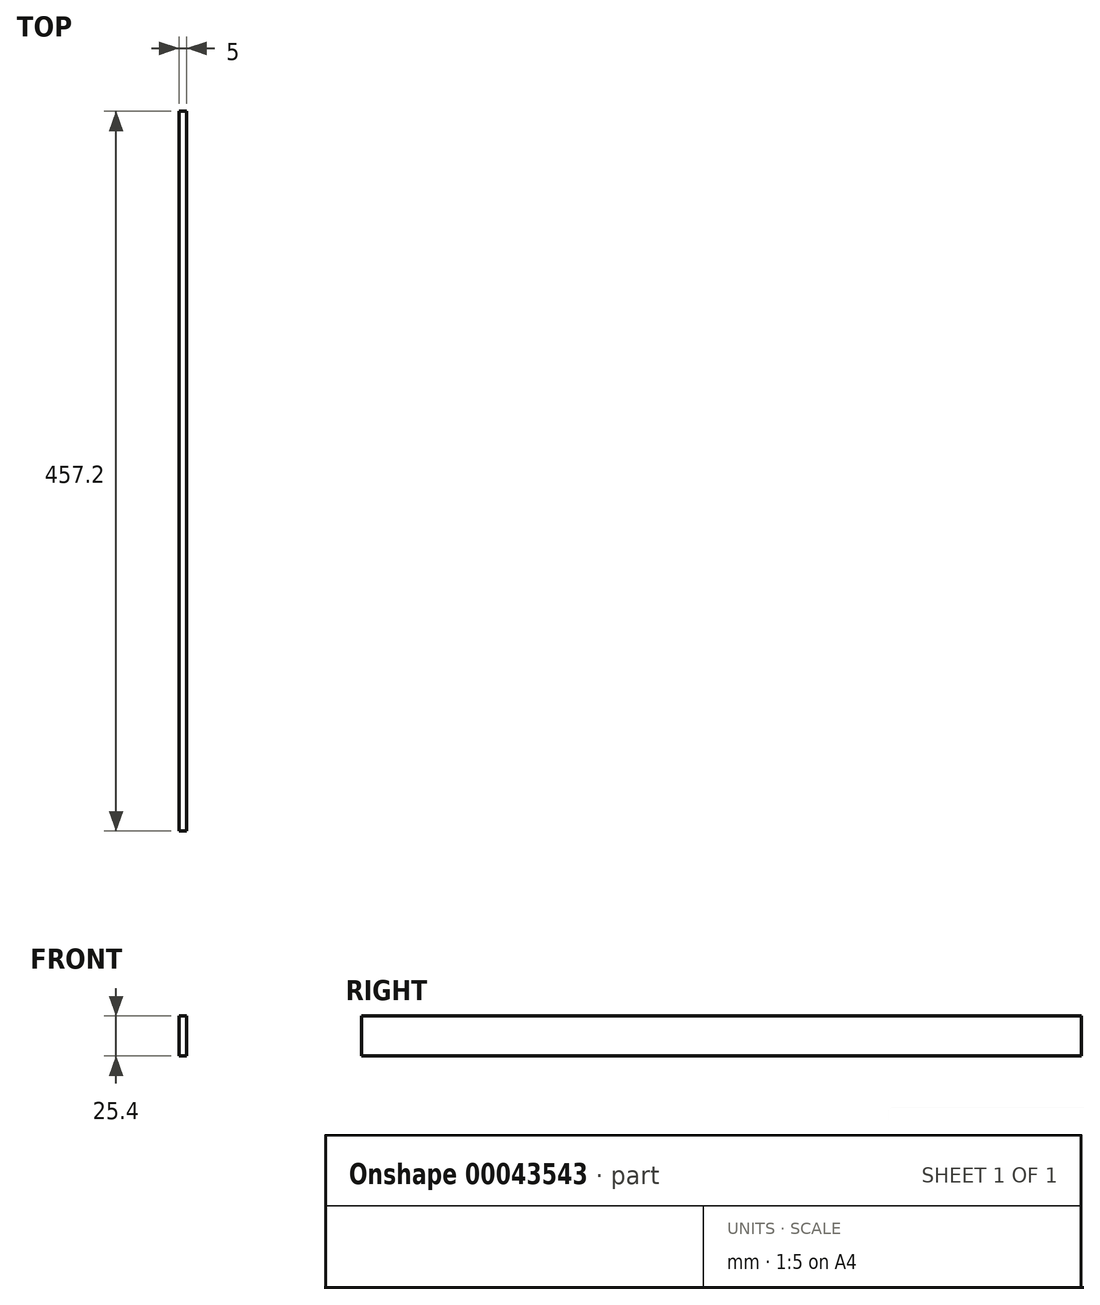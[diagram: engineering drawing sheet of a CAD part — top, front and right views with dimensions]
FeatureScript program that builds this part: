
annotation { "Feature Type Name" : "Feature", "Feature Type Description" : "" }
export const myFeature = defineFeature(function(context is Context, id is Id, definition is map)
    precondition{}
    {
        {
            var Q0;
            Q0=qCreatedBy(makeId("Right.planeOp"),FACE);
            var sketch = newSketch(context, id + "F0", { "sketchPlane" : qUnion([Q0])});
            skLineSegment(sketch, "E0.rect.bottom", {"start": v(228.6, 12.7) * mm, "end": v(-228.6, 12.7) * mm});
            skLineSegment(sketch, "E0.rect.top", {"start": v(228.6, -12.7) * mm, "end": v(-228.6, -12.7) * mm});
            skLineSegment(sketch, "E0.rect.left", {"start": v(228.6, 12.7) * mm, "end": v(228.6, -12.7) * mm});
            skLineSegment(sketch, "E0.rect.right", {"start": v(-228.6, 12.7) * mm, "end": v(-228.6, -12.7) * mm});
            skPoint(sketch, "E0.rect.middle", {"position": v(0, 0) * mm});
            skSolve(sketch);
        }
        {
            var Q0;
            Q0=makeQuery(id+"F0.imprint","IMPRINT",FACE,{"disambiguationData":[TD([[makeQuery(id+"F0.imprint","IMPRINT",EDGE,{"derivedFrom":sQuery(id+"F0.wireOp",EDGE,"E0.rect.bottom")}),1.0]])]});
            extrude(context, id + "F1", {"entities" : qUnion([Q0]), "oppositeDirection" : true, "depth" : 5 * mm});
        }
    });
